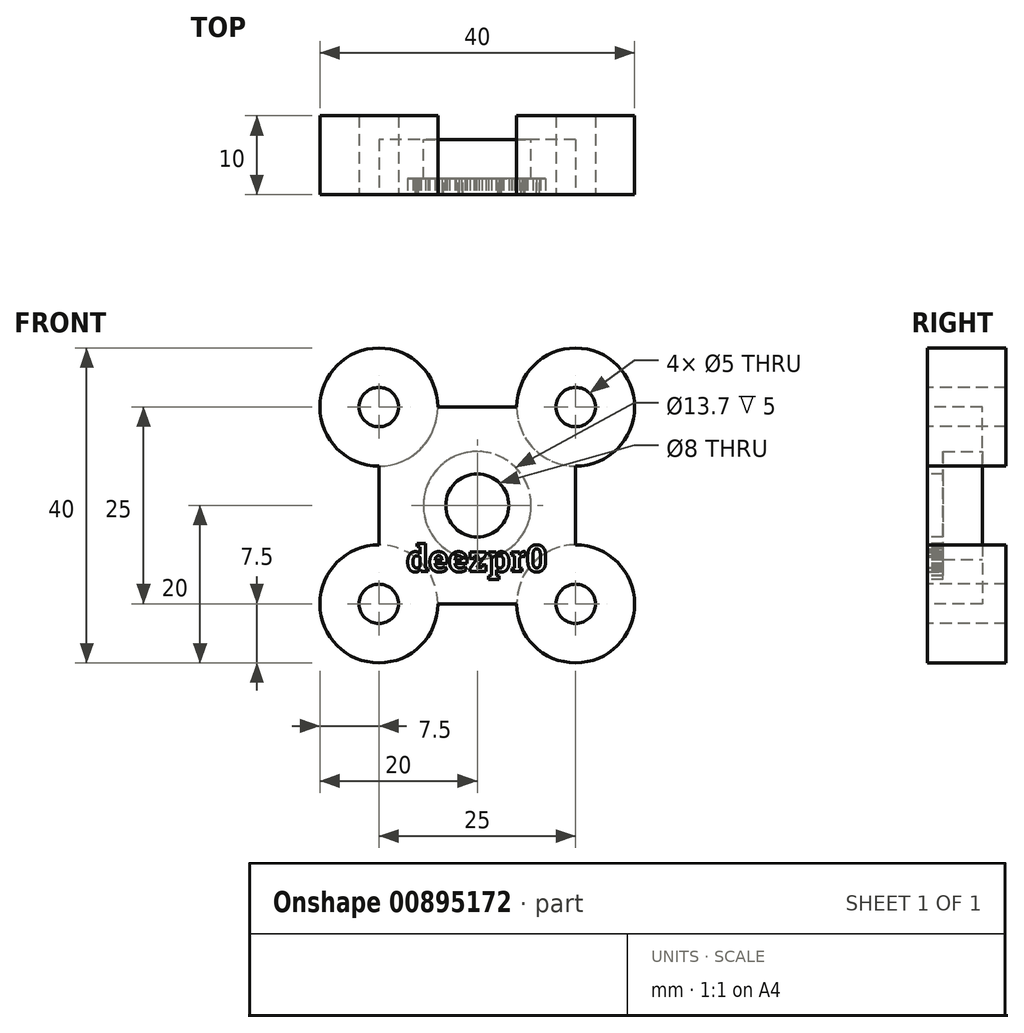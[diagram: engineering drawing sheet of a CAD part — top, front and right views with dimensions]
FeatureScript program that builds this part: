
annotation { "Feature Type Name" : "Feature", "Feature Type Description" : "" }
export const myFeature = defineFeature(function(context is Context, id is Id, definition is map)
    precondition{}
    {
        {
            var Q0;
            Q0=qCreatedBy(makeId("Front.planeOp"),FACE);
            var sketch = newSketch(context, id + "F0", { "sketchPlane" : qUnion([Q0])});
            skLineSegment(sketch, "E0.bottom", {"start": v(12.5, 12.5) * mm, "end": v(-12.5, 12.5) * mm});
            skLineSegment(sketch, "E0.top", {"start": v(12.5, -12.5) * mm, "end": v(-12.5, -12.5) * mm});
            skLineSegment(sketch, "E0.left", {"start": v(12.5, 12.5) * mm, "end": v(12.5, -12.5) * mm});
            skLineSegment(sketch, "E0.right", {"start": v(-12.5, 12.5) * mm, "end": v(-12.5, -12.5) * mm});
            skPoint(sketch, "E0.middle", {"position": v(0, 0) * mm});
            skSolve(sketch);
        }
        {
            var Q0;
            Q0=makeQuery(id+"F0.imprint","IMPRINT",FACE,{"disambiguationData":[TD([[makeQuery(id+"F0.imprint","IMPRINT",EDGE,{"derivedFrom":sQuery(id+"F0.wireOp",EDGE,"E0.bottom")}),1.0]])]});
            extrude(context, id + "F1", {"entities" : qUnion([Q0]), "depth" : 7 * mm, "offsetDistance" : 25 * mm});
        }
        {
            var Q0;
            Q0=makeQuery(id+"F1.opExtrude","CAP_FACE",FACE,{"disambiguationData":[OSD([sQuery(id+"F0.wireOp",EDGE,"E0.bottom"),sQuery(id+"F0.wireOp",EDGE,"E0.top"),sQuery(id+"F0.wireOp",EDGE,"E0.left"),sQuery(id+"F0.wireOp",EDGE,"E0.right")])],"isStart":true});
            var sketch = newSketch(context, id + "F2", { "sketchPlane" : qUnion([Q0])});
            skCircle(sketch, "E1", {"center": v(0, 0) * mm, "radius": 6.85 * mm});
            skSolve(sketch);
        }
        {
            var Q0;
            Q0=makeQuery(id+"F2.imprint","IMPRINT",FACE,{"disambiguationData":[TD([[makeQuery(id+"F2.imprint","IMPRINT",EDGE,{"derivedFrom":sQuery(id+"F2.wireOp",EDGE,"E1")}),1.0]])]});
            extrude(context, id + "F3", {"entities" : qUnion([Q0]), "operationType" : NewBodyOperationType.REMOVE, "oppositeDirection" : true, "depth" : 5 * mm, "offsetDistance" : 25 * mm});
        }
        {
            var Q0;
            Q0=makeQuery(id+"F1.opExtrude","CAP_FACE",FACE,{"disambiguationData":[OSD([sQuery(id+"F0.wireOp",EDGE,"E0.bottom"),sQuery(id+"F0.wireOp",EDGE,"E0.top"),sQuery(id+"F0.wireOp",EDGE,"E0.left"),sQuery(id+"F0.wireOp",EDGE,"E0.right")])],"isStart":false});
            var sketch = newSketch(context, id + "F4", { "sketchPlane" : qUnion([Q0])});
            skCircle(sketch, "E2", {"center": v(0, 0) * mm, "radius": 4 * mm});
            skSolve(sketch);
        }
        {
            var Q0;
            Q0=makeQuery(id+"F4.imprint","IMPRINT",FACE,{"disambiguationData":[TD([[makeQuery(id+"F4.imprint","IMPRINT",EDGE,{"derivedFrom":sQuery(id+"F4.wireOp",EDGE,"E2")}),1.0]])]});
            extrude(context, id + "F5", {"entities" : qUnion([Q0]), "operationType" : NewBodyOperationType.REMOVE, "oppositeDirection" : true, "depth" : 25 * mm, "offsetDistance" : 25 * mm});
        }
        {
            var Q0;
            Q0=makeQuery(id+"F1.opExtrude","CAP_FACE",FACE,{"disambiguationData":[OSD([sQuery(id+"F0.wireOp",EDGE,"E0.bottom"),sQuery(id+"F0.wireOp",EDGE,"E0.top"),sQuery(id+"F0.wireOp",EDGE,"E0.left"),sQuery(id+"F0.wireOp",EDGE,"E0.right")])],"isStart":false});
            var sketch = newSketch(context, id + "F6", { "sketchPlane" : qUnion([Q0])});
            skCircle(sketch, "E3", {"center": v(-12.5, 12.5) * mm, "radius": 7.5 * mm});
            skCircle(sketch, "E4", {"center": v(12.5, 12.5) * mm, "radius": 7.5 * mm});
            skCircle(sketch, "E5", {"center": v(-12.5, -12.5) * mm, "radius": 7.5 * mm});
            skCircle(sketch, "E6", {"center": v(12.5, -12.5) * mm, "radius": 7.5 * mm});
            skSolve(sketch);
        }
        {
            var Q0;
            {var subQ0=sQuery(id+"F6.wireOp",EDGE,"E3");var subQ1=makeQuery(id+"F1.opExtrude","CAP_EDGE",EDGE,{"disambiguationData":[OSD([sQuery(id+"F0.wireOp",EDGE,"E0.bottom")])],"isStart":false});var subQ2=makeQuery(id+"F6.imprint","INTERSECT",VERTEX,{"derivedFrom":[subQ1,subQ0]});Q0=makeQuery(id+"F6.imprint","IMPRINT",FACE,{"disambiguationData":[TD([[makeQuery(id+"F6.imprint","IMPRINT",EDGE,{"disambiguationData":[TD([[subQ2,-1.0]])],"derivedFrom":subQ0}),1.0]])]});}
            var Q1;
            {var subQ0=sQuery(id+"F6.wireOp",EDGE,"E3");var subQ1=makeQuery(id+"F1.opExtrude","CAP_EDGE",EDGE,{"disambiguationData":[OSD([sQuery(id+"F0.wireOp",EDGE,"E0.bottom")])],"isStart":false});var subQ2=makeQuery(id+"F6.imprint","INTERSECT",VERTEX,{"derivedFrom":[subQ1,subQ0]});Q1=makeQuery(id+"F6.imprint","IMPRINT",FACE,{"disambiguationData":[TD([[makeQuery(id+"F6.imprint","IMPRINT",EDGE,{"disambiguationData":[TD([[subQ2,1.0]])],"derivedFrom":subQ0}),1.0]])]});}
            var Q2;
            {var subQ0=sQuery(id+"F6.wireOp",EDGE,"E4");var subQ1=makeQuery(id+"F1.opExtrude","CAP_EDGE",EDGE,{"disambiguationData":[OSD([sQuery(id+"F0.wireOp",EDGE,"E0.bottom")])],"isStart":false});var subQ2=makeQuery(id+"F6.imprint","INTERSECT",VERTEX,{"derivedFrom":[subQ1,subQ0]});Q2=makeQuery(id+"F6.imprint","IMPRINT",FACE,{"disambiguationData":[TD([[makeQuery(id+"F6.imprint","IMPRINT",EDGE,{"disambiguationData":[TD([[subQ2,-1.0]])],"derivedFrom":subQ0}),1.0]])]});}
            var Q3;
            {var subQ0=sQuery(id+"F6.wireOp",EDGE,"E4");var subQ1=makeQuery(id+"F1.opExtrude","CAP_EDGE",EDGE,{"disambiguationData":[OSD([sQuery(id+"F0.wireOp",EDGE,"E0.bottom")])],"isStart":false});var subQ2=makeQuery(id+"F6.imprint","INTERSECT",VERTEX,{"derivedFrom":[subQ1,subQ0]});Q3=makeQuery(id+"F6.imprint","IMPRINT",FACE,{"disambiguationData":[TD([[makeQuery(id+"F6.imprint","IMPRINT",EDGE,{"disambiguationData":[TD([[subQ2,1.0]])],"derivedFrom":subQ0}),1.0]])]});}
            var Q4;
            {var subQ0=sQuery(id+"F6.wireOp",EDGE,"E6");var subQ1=makeQuery(id+"F1.opExtrude","CAP_EDGE",EDGE,{"disambiguationData":[OSD([sQuery(id+"F0.wireOp",EDGE,"E0.top")])],"isStart":false});var subQ2=makeQuery(id+"F6.imprint","INTERSECT",VERTEX,{"derivedFrom":[subQ1,subQ0]});Q4=makeQuery(id+"F6.imprint","IMPRINT",FACE,{"disambiguationData":[TD([[makeQuery(id+"F6.imprint","IMPRINT",EDGE,{"disambiguationData":[TD([[subQ2,-1.0]])],"derivedFrom":subQ0}),1.0]])]});}
            var Q5;
            {var subQ0=sQuery(id+"F6.wireOp",EDGE,"E6");var subQ1=makeQuery(id+"F1.opExtrude","CAP_EDGE",EDGE,{"disambiguationData":[OSD([sQuery(id+"F0.wireOp",EDGE,"E0.top")])],"isStart":false});var subQ2=makeQuery(id+"F6.imprint","INTERSECT",VERTEX,{"derivedFrom":[subQ1,subQ0]});Q5=makeQuery(id+"F6.imprint","IMPRINT",FACE,{"disambiguationData":[TD([[makeQuery(id+"F6.imprint","IMPRINT",EDGE,{"disambiguationData":[TD([[subQ2,1.0]])],"derivedFrom":subQ0}),1.0]])]});}
            var Q6;
            {var subQ0=sQuery(id+"F6.wireOp",EDGE,"E5");var subQ1=makeQuery(id+"F1.opExtrude","CAP_EDGE",EDGE,{"disambiguationData":[OSD([sQuery(id+"F0.wireOp",EDGE,"E0.top")])],"isStart":false});var subQ2=makeQuery(id+"F6.imprint","INTERSECT",VERTEX,{"derivedFrom":[subQ1,subQ0]});Q6=makeQuery(id+"F6.imprint","IMPRINT",FACE,{"disambiguationData":[TD([[makeQuery(id+"F6.imprint","IMPRINT",EDGE,{"disambiguationData":[TD([[subQ2,-1.0]])],"derivedFrom":subQ0}),1.0]])]});}
            var Q7;
            {var subQ0=sQuery(id+"F6.wireOp",EDGE,"E5");var subQ1=makeQuery(id+"F1.opExtrude","CAP_EDGE",EDGE,{"disambiguationData":[OSD([sQuery(id+"F0.wireOp",EDGE,"E0.top")])],"isStart":false});var subQ2=makeQuery(id+"F6.imprint","INTERSECT",VERTEX,{"derivedFrom":[subQ1,subQ0]});Q7=makeQuery(id+"F6.imprint","IMPRINT",FACE,{"disambiguationData":[TD([[makeQuery(id+"F6.imprint","IMPRINT",EDGE,{"disambiguationData":[TD([[subQ2,1.0]])],"derivedFrom":subQ0}),1.0]])]});}
            extrude(context, id + "F7", {"entities" : qUnion([Q0, Q1, Q2, Q3, Q4, Q5, Q6, Q7]), "operationType" : NewBodyOperationType.ADD, "oppositeDirection" : true, "depth" : 10 * mm, "offsetDistance" : 25 * mm});
        }
        {
            var Q0;
            Q0=makeQuery(id+"F7.boolean.opBoolean","MERGE",FACE,{"derivedFrom":[makeQuery(id+"F1.opExtrude","CAP_FACE",FACE,{"disambiguationData":[OSD([sQuery(id+"F0.wireOp",EDGE,"E0.bottom"),sQuery(id+"F0.wireOp",EDGE,"E0.top"),sQuery(id+"F0.wireOp",EDGE,"E0.left"),sQuery(id+"F0.wireOp",EDGE,"E0.right")])],"isStart":false}),makeQuery(id+"F7.opExtrude","CAP_FACE",FACE,{"disambiguationData":[OSD([sQuery(id+"F6.wireOp",EDGE,"E3")])],"isStart":true}),makeQuery(id+"F7.opExtrude","CAP_FACE",FACE,{"disambiguationData":[OSD([sQuery(id+"F6.wireOp",EDGE,"E4")])],"isStart":true}),makeQuery(id+"F7.opExtrude","CAP_FACE",FACE,{"disambiguationData":[OSD([sQuery(id+"F6.wireOp",EDGE,"E5")])],"isStart":true}),makeQuery(id+"F7.opExtrude","CAP_FACE",FACE,{"disambiguationData":[OSD([sQuery(id+"F6.wireOp",EDGE,"E6")])],"isStart":true})]});
            var sketch = newSketch(context, id + "F8", { "sketchPlane" : qUnion([Q0])});
            skCircle(sketch, "E7", {"center": v(-12.5, 12.5) * mm, "radius": 2.5 * mm});
            skCircle(sketch, "E8", {"center": v(12.5, 12.5) * mm, "radius": 2.5 * mm});
            skCircle(sketch, "E9", {"center": v(-12.5, -12.5) * mm, "radius": 2.5 * mm});
            skCircle(sketch, "E10", {"center": v(12.5, -12.5) * mm, "radius": 2.5 * mm});
            skSolve(sketch);
        }
        {
            var Q0;
            Q0=makeQuery(id+"F8.imprint","IMPRINT",FACE,{"disambiguationData":[TD([[makeQuery(id+"F8.imprint","IMPRINT",EDGE,{"derivedFrom":sQuery(id+"F8.wireOp",EDGE,"E8")}),1.0]])]});
            var Q1;
            Q1=makeQuery(id+"F8.imprint","IMPRINT",FACE,{"disambiguationData":[TD([[makeQuery(id+"F8.imprint","IMPRINT",EDGE,{"derivedFrom":sQuery(id+"F8.wireOp",EDGE,"E10")}),1.0]])]});
            var Q2;
            Q2=makeQuery(id+"F8.imprint","IMPRINT",FACE,{"disambiguationData":[TD([[makeQuery(id+"F8.imprint","IMPRINT",EDGE,{"derivedFrom":sQuery(id+"F8.wireOp",EDGE,"E7")}),1.0]])]});
            var Q3;
            Q3=makeQuery(id+"F8.imprint","IMPRINT",FACE,{"disambiguationData":[TD([[makeQuery(id+"F8.imprint","IMPRINT",EDGE,{"derivedFrom":sQuery(id+"F8.wireOp",EDGE,"E9")}),1.0]])]});
            extrude(context, id + "F9", {"entities" : qUnion([Q0, Q1, Q2, Q3]), "operationType" : NewBodyOperationType.REMOVE, "oppositeDirection" : true, "depth" : 25 * mm, "offsetDistance" : 25 * mm});
        }
        {
            var Q0;
            Q0=makeQuery(id+"F7.boolean.opBoolean","MERGE",FACE,{"derivedFrom":[makeQuery(id+"F1.opExtrude","CAP_FACE",FACE,{"disambiguationData":[OSD([sQuery(id+"F0.wireOp",EDGE,"E0.bottom"),sQuery(id+"F0.wireOp",EDGE,"E0.top"),sQuery(id+"F0.wireOp",EDGE,"E0.left"),sQuery(id+"F0.wireOp",EDGE,"E0.right")])],"isStart":false}),makeQuery(id+"F7.opExtrude","CAP_FACE",FACE,{"disambiguationData":[OSD([sQuery(id+"F6.wireOp",EDGE,"E3")])],"isStart":true}),makeQuery(id+"F7.opExtrude","CAP_FACE",FACE,{"disambiguationData":[OSD([sQuery(id+"F6.wireOp",EDGE,"E4")])],"isStart":true}),makeQuery(id+"F7.opExtrude","CAP_FACE",FACE,{"disambiguationData":[OSD([sQuery(id+"F6.wireOp",EDGE,"E5")])],"isStart":true}),makeQuery(id+"F7.opExtrude","CAP_FACE",FACE,{"disambiguationData":[OSD([sQuery(id+"F6.wireOp",EDGE,"E6")])],"isStart":true})]});
            var sketch = newSketch(context, id + "F10", { "sketchPlane" : qUnion([Q0])});
            skText(sketch, "E11", { "text": "deezpr0", "fontName": "RobotoSlab-Bold.ttf"});
            const initialGuessF10  = {"E11": [-0.009, -0.00841, 1, 0, 0.00341]};
            skSetInitialGuess(sketch, initialGuessF10);
            skSolve(sketch);
        }
        {
            var Q0;
            Q0 = qSketchRegion(id + "F10", true);
            extrude(context, id + "F11", {"entities" : qUnion([Q0]), "operationType" : NewBodyOperationType.REMOVE, "oppositeDirection" : true, "depth" : 2 * mm, "offsetDistance" : 25 * mm});
        }
    });
